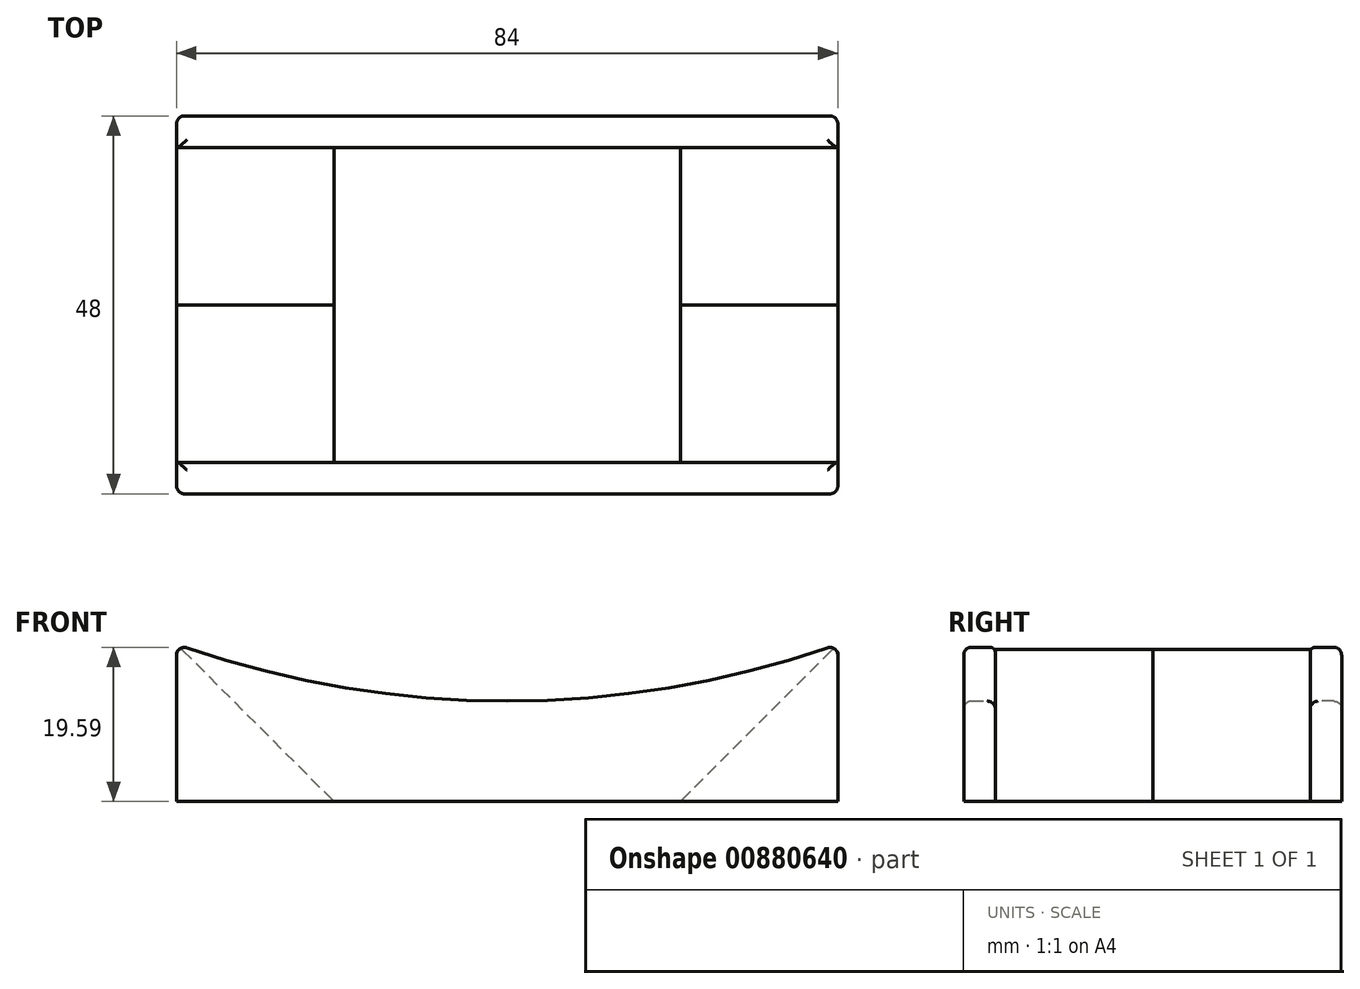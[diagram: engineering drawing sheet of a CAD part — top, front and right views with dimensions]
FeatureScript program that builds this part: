
annotation { "Feature Type Name" : "Feature", "Feature Type Description" : "" }
export const myFeature = defineFeature(function(context is Context, id is Id, definition is map)
    precondition{}
    {
        {
            var Q0;
            Q0=qCreatedBy(makeId("Front.planeOp"),FACE);
            var sketch = newSketch(context, id + "F0", { "sketchPlane" : qUnion([Q0])});
            skLineSegment(sketch, "E0", {"start": v(-42, 0) * mm, "end": v(-42, 20) * mm});
            skLineSegment(sketch, "E1", {"start": v(-42, 20) * mm, "end": v(-22, 0) * mm});
            skLineSegment(sketch, "E2", {"start": v(-22, 0) * mm, "end": v(-42, 0) * mm});
            skLineSegment(sketch, "E3.MirrorCS", {"start": v(22, 0) * mm, "end": v(42, 0) * mm});
            skLineSegment(sketch, "E4.MirrorCS", {"start": v(42, 20) * mm, "end": v(22, 0) * mm});
            skLineSegment(sketch, "E5.MirrorCS", {"start": v(42, 0) * mm, "end": v(42, 20) * mm});
            skSolve(sketch);
        }
        {
            var Q0;
            Q0=makeQuery(id+"F0.imprint","IMPRINT",FACE,{"disambiguationData":[TD([[makeQuery(id+"F0.imprint","IMPRINT",EDGE,{"derivedFrom":sQuery(id+"F0.wireOp",EDGE,"E0")}),-1.0]])]});
            var Q1;
            Q1=makeQuery(id+"F0.imprint","IMPRINT",FACE,{"disambiguationData":[TD([[makeQuery(id+"F0.imprint","IMPRINT",EDGE,{"derivedFrom":sQuery(id+"F0.wireOp",EDGE,"E3.MirrorCS")}),1.0]])]});
            extrude(context, id + "F1", {"entities" : qUnion([Q0, Q1]), "oppositeDirection" : true, "depth" : 20 * mm, "offsetDistance" : 25 * mm});
        }
        {
            var Q0;
            Q0=makeQuery(id+"F1.opExtrude","CAP_FACE",FACE,{"disambiguationData":[OSD([sQuery(id+"F0.wireOp",EDGE,"E3.MirrorCS"),sQuery(id+"F0.wireOp",EDGE,"E4.MirrorCS"),sQuery(id+"F0.wireOp",EDGE,"E5.MirrorCS")])],"isStart":false});
            var sketch = newSketch(context, id + "F2", { "sketchPlane" : qUnion([Q0])});
            skLineSegment(sketch, "E6", {"start": v(-42, 20) * mm, "end": v(-42, 0) * mm});
            skLineSegment(sketch, "E7", {"start": v(-42, 0) * mm, "end": v(42, 0) * mm});
            skLineSegment(sketch, "E8", {"start": v(42, 0) * mm, "end": v(42, 20) * mm});
            skArc(sketch, "E9", {"start": v(-42, 20) * mm, "mid": v(0, 12.75) * mm, "end": v(42, 20) * mm});
            skSolve(sketch);
        }
        {
            var Q0;
            {var subQ0=sQuery(id+"F2.wireOp",EDGE,"E6");Q0=makeQuery(id+"F2.imprint","IMPRINT",FACE,{"disambiguationData":[TD([[makeQuery(id+"F2.imprint","IMPRINT",EDGE,{"derivedFrom":subQ0}),-1.0]])]});}
            var Q1;
            {var subQ2=sQuery(id+"F2.wireOp",EDGE,"E8");Q1=makeQuery(id+"F2.imprint","IMPRINT",FACE,{"disambiguationData":[TD([[makeQuery(id+"F2.imprint","IMPRINT",EDGE,{"derivedFrom":subQ2}),1.0]])]});}
            extrude(context, id + "F3", {"entities" : qUnion([Q0, Q1]), "depth" : 4 * mm, "offsetDistance" : 25 * mm});
        }
        {
            var Q0;
            Q0=makeQuery(id+"F3.opExtrude","SWEPT_FACE",FACE,{"disambiguationData":[OSD([sQuery(id+"F2.wireOp",EDGE,"E9")])]});
            var Q1;
            Q1=makeQuery(id+"F3.opExtrude","CAP_EDGE",EDGE,{"disambiguationData":[OSD([sQuery(id+"F2.wireOp",EDGE,"E6")])],"isStart":false});
            var Q2;
            Q2=makeQuery(id+"F3.opExtrude","CAP_EDGE",EDGE,{"disambiguationData":[OSD([sQuery(id+"F2.wireOp",EDGE,"E8")])],"isStart":false});
            fillet(context, id + "F4", {"entities" : qUnion([Q0, Q1, Q2]), "radius" : 1 * mm, "tangentPropagation" : true, "allowEdgeOverflow" : false});
        }
        {
            var Q0;
            Q0=makeQuery(id+"F1.opExtrude","SWEPT_EDGE",EDGE,{"disambiguationData":[OSD([sQuery(id+"F0.wireOp",EDGE,"E4.MirrorCS"),sQuery(id+"F0.wireOp",EDGE,"E5.MirrorCS")])]});
            var Q1;
            Q1=makeQuery(id+"F1.opExtrude","SWEPT_EDGE",EDGE,{"disambiguationData":[OSD([sQuery(id+"F0.wireOp",EDGE,"E0"),sQuery(id+"F0.wireOp",EDGE,"E1")])]});
            fillet(context, id + "F5", {"entities" : qUnion([Q0, Q1]), "radius" : .5 * mm, "tangentPropagation" : true, "allowEdgeOverflow" : false});
        }
        {
            var Q0;
            Q0=makeQuery(id+"F1.opExtrude","SWEPT_BODY",BODY,{"disambiguationData":[OSD([sQuery(id+"F0.wireOp",EDGE,"E0"),sQuery(id+"F0.wireOp",EDGE,"E1"),sQuery(id+"F0.wireOp",EDGE,"E2")])]});
            var Q1;
            Q1=makeQuery(id+"F1.opExtrude","SWEPT_BODY",BODY,{"disambiguationData":[OSD([sQuery(id+"F0.wireOp",EDGE,"E3.MirrorCS"),sQuery(id+"F0.wireOp",EDGE,"E4.MirrorCS"),sQuery(id+"F0.wireOp",EDGE,"E5.MirrorCS")])]});
            var Q2;
            Q2=makeQuery(id+"F3.opExtrude","SWEPT_BODY",BODY,{"disambiguationData":[OSD([sQuery(id+"F2.wireOp",EDGE,"E6"),sQuery(id+"F2.wireOp",EDGE,"E7"),sQuery(id+"F2.wireOp",EDGE,"E8"),sQuery(id+"F2.wireOp",EDGE,"E9")])]});
            var Q3;
            Q3=qCreatedBy(makeId("Front.planeOp"),FACE);
            mirror(context, id + "F6", {"entities" : qUnion([Q0, Q1, Q2]), "mirrorPlane" : qUnion([Q3])});
        }
    });
